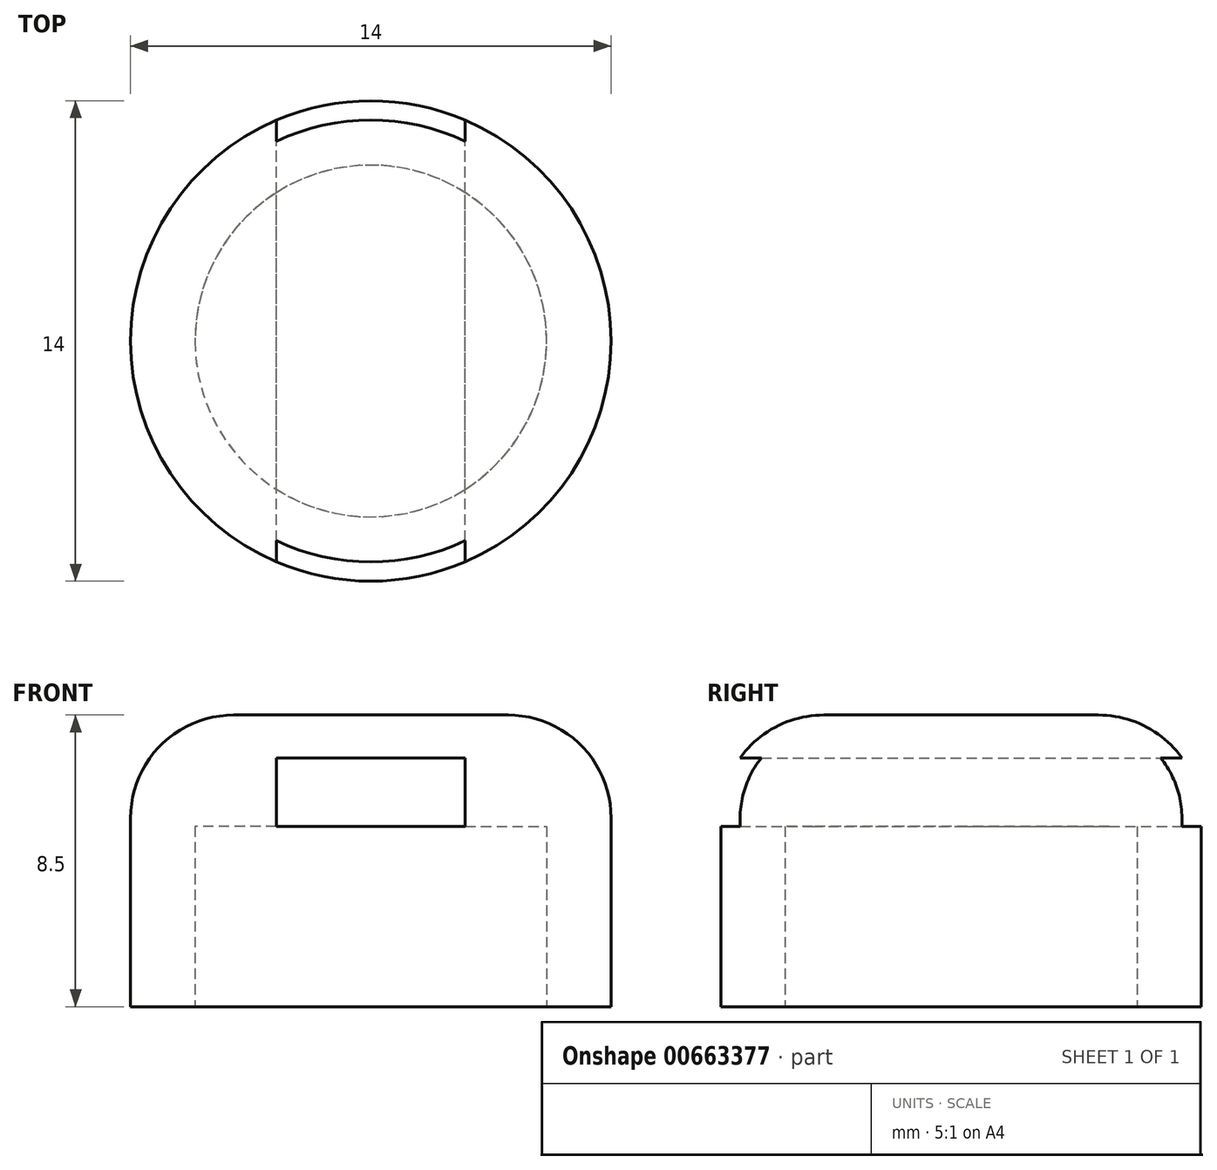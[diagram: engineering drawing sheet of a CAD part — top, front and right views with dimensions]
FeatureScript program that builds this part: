
annotation { "Feature Type Name" : "Feature", "Feature Type Description" : "" }
export const myFeature = defineFeature(function(context is Context, id is Id, definition is map)
    precondition{}
    {
        {
            var Q0;
            Q0=qCreatedBy(makeId("Front.planeOp"),FACE);
            var sketch = newSketch(context, id + "F0", { "sketchPlane" : qUnion([Q0])});
            skLineSegment(sketch, "E0", {"start": v(0, 0) * mm, "end": v(7, 0) * mm});
            skLineSegment(sketch, "E1", {"start": v(7, 0) * mm, "end": v(7, 5.5) * mm});
            skLineSegment(sketch, "E2", {"start": v(0, 0) * mm, "end": v(0, 8.5) * mm});
            skLineSegment(sketch, "E3", {"start": v(0, 8.5) * mm, "end": v(4, 8.5) * mm});
            skLineSegment(sketch, "E4", {"start": v(0, -6.1) * mm, "end": v(0, 11.18) * mm, "construction": true});
            skPoint(sketch, "E5.visualSharp", {"position": v(7, 8.5) * mm});
            skArc(sketch, "E5.filletArc", {"start": v(7, 5.5) * mm, "mid": v(6.12, 7.62) * mm, "end": v(4, 8.5) * mm});
            skSolve(sketch);
        }
        {
            var Q0;
            Q0=makeQuery(id+"F0.imprint","IMPRINT",FACE,{"disambiguationData":[TD([[makeQuery(id+"F0.imprint","IMPRINT",EDGE,{"derivedFrom":sQuery(id+"F0.wireOp",EDGE,"E0")}),1.0]])]});
            var Q1;
            Q1=sQuery(id+"F0.wireOp",EDGE,"E4");
            revolve(context, id + "F1", {"entities" : qUnion([Q0]), "axis" : qUnion([Q1]), "revolveType" : RevolveType.FULL});
        }
        {
            var Q0;
            Q0=makeQuery(id+"F1.opRevolve","SWEPT_FACE",FACE,{"disambiguationData":[OSD([sQuery(id+"F0.wireOp",EDGE,"E0")])]});
            var sketch = newSketch(context, id + "F2", { "sketchPlane" : qUnion([Q0])});
            skCircle(sketch, "E6", {"center": v(0, 0) * mm, "radius": 5.12 * mm});
            skSolve(sketch);
        }
        {
            var Q0;
            Q0 = qSketchRegion(id + "F2", true);
            extrude(context, id + "F3", {"entities" : qUnion([Q0]), "operationType" : NewBodyOperationType.REMOVE, "oppositeDirection" : true, "depth" : 5.25 * mm, "offsetDistance" : 25 * mm});
        }
        {
            var Q0;
            Q0=qCreatedBy(makeId("Front.planeOp"),FACE);
            var sketch = newSketch(context, id + "F4", { "sketchPlane" : qUnion([Q0])});
            skLineSegment(sketch, "E7.0", {"start": v(5.12, 5.25) * mm, "end": v(-5.12, 5.25) * mm});
            skLineSegment(sketch, "E8", {"start": v(-2.75, 5.25) * mm, "end": v(-2.75, 7.25) * mm});
            skLineSegment(sketch, "E9", {"start": v(-2.75, 7.25) * mm, "end": v(2.75, 7.25) * mm});
            skLineSegment(sketch, "E10", {"start": v(2.75, 7.25) * mm, "end": v(2.75, 5.25) * mm});
            skLineSegment(sketch, "E11", {"start": v(2.75, 5.25) * mm, "end": v(-2.75, 5.25) * mm});
            skSolve(sketch);
        }
        {
            var Q0;
            Q0=makeQuery(id+"F4.imprint","IMPRINT",FACE,{"disambiguationData":[TD([[makeQuery(id+"F4.imprint","IMPRINT",EDGE,{"derivedFrom":sQuery(id+"F4.wireOp",EDGE,"E8")}),-1.0]])]});
            extrude(context, id + "F5", {"entities" : qUnion([Q0]), "operationType" : NewBodyOperationType.REMOVE, "endBound" : BoundingType.SYMMETRIC, "depth" : 15 * mm, "offsetDistance" : 25 * mm});
        }
    });
